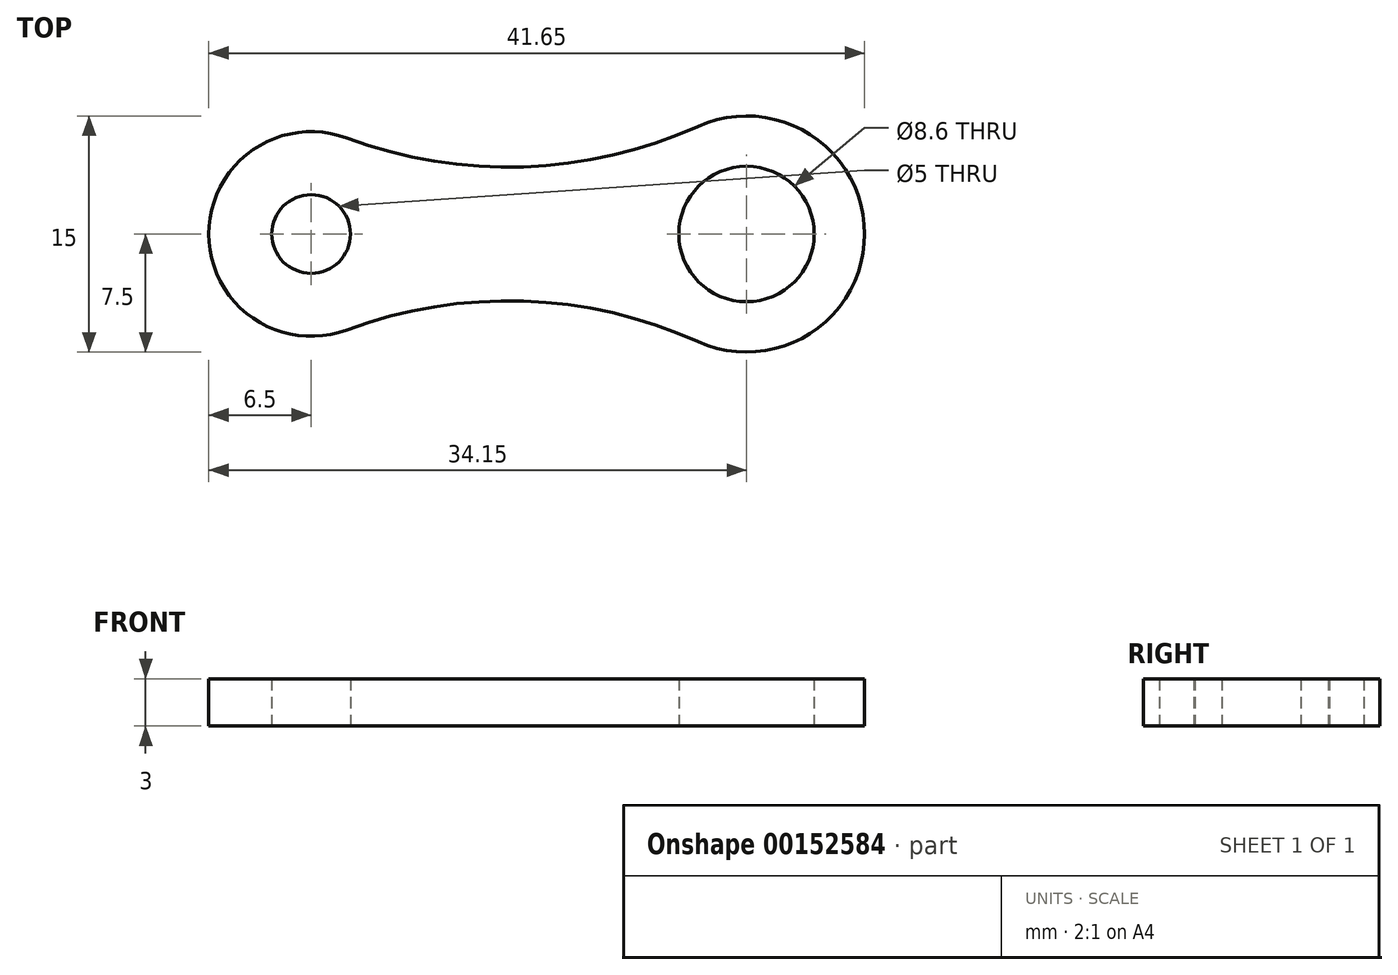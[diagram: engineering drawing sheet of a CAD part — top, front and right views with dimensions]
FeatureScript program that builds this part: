
annotation { "Feature Type Name" : "Feature", "Feature Type Description" : "" }
export const myFeature = defineFeature(function(context is Context, id is Id, definition is map)
    precondition{}
    {
        {
            var Q0;
            Q0=qCreatedBy(makeId("Top.planeOp"),FACE);
            var sketch = newSketch(context, id + "F0", { "sketchPlane" : qUnion([Q0])});
            skLineSegment(sketch, "E0", {"start": v(0, 0) * mm, "end": v(20.85, 0) * mm, "construction": true});
            skCircle(sketch, "E1", {"center": v(25.15, 0) * mm, "radius": 4.3 * mm});
            skCircle(sketch, "E2", {"center": v(25.15, 0) * mm, "radius": 7.5 * mm});
            skCircle(sketch, "E3", {"center": v(-2.5, 0) * mm, "radius": 2.5 * mm});
            skCircle(sketch, "E4", {"center": v(-2.5, 0) * mm, "radius": 6.5 * mm});
            skLineSegment(sketch, "E5", {"start": v(10.43, 0) * mm, "end": v(10.43, 4.25) * mm, "construction": true});
            skLineSegment(sketch, "E6.MirrorCS", {"start": v(10.43, 0) * mm, "end": v(10.43, -4.25) * mm, "construction": true});
            skArc(sketch, "E7", {"start": v(-0.23, 6.1) * mm, "mid": v(11, 4.26) * mm, "end": v(22.07, 6.84) * mm});
            skArc(sketch, "E8.MirrorCS", {"start": v(-0.23, -6.1) * mm, "mid": v(11, -4.26) * mm, "end": v(22.07, -6.84) * mm});
            skSolve(sketch);
        }
        {
            var Q0;
            Q0 = qSketchRegion(id + "F0", true);
            extrude(context, id + "F1", {"entities" : qUnion([Q0]), "depth" : 3 * mm});
        }
    });
